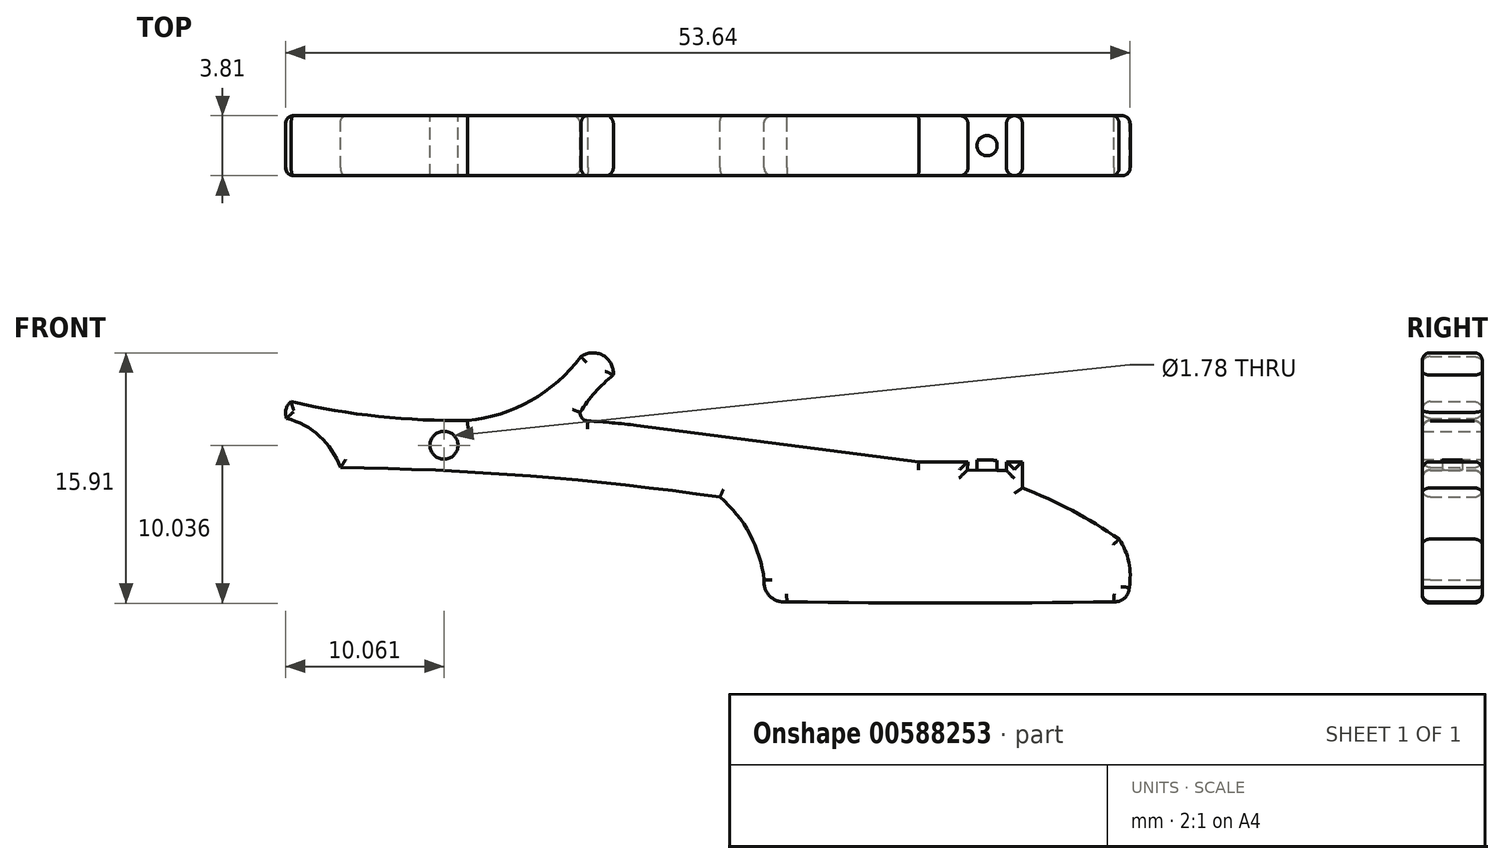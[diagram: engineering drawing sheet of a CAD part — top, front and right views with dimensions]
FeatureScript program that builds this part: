
annotation { "Feature Type Name" : "Feature", "Feature Type Description" : "" }
export const myFeature = defineFeature(function(context is Context, id is Id, definition is map)
    precondition{}
    {
        {
            var Q0;
            Q0=qCreatedBy(makeId("Front.planeOp"),FACE);
            var sketch = newSketch(context, id + "F0", { "sketchPlane" : qUnion([Q0])});
            skLineSegment(sketch, "E0", {"start": v(-47.34, 18.05) * mm, "end": v(-47.34, 18.05) * mm});
            skPoint(sketch, "E1", {"position": v(-38.73, 22.02) * mm});
            skArc(sketch, "E2", {"start": v(-38.9, 20.92) * mm, "mid": v(-39.55, 22.17) * mm, "end": v(-40.95, 22.1) * mm});
            skArc(sketch, "E3", {"start": v(-29.32, 7.9) * mm, "mid": v(-30.22, 10.8) * mm, "end": v(-32.13, 13.17) * mm});
            skArc(sketch, "E4", {"start": v(-29.32, 7.9) * mm, "mid": v(-28.93, 6.85) * mm, "end": v(-27.86, 6.53) * mm});
            skArc(sketch, "E5", {"start": v(-27.86, 6.53) * mm, "mid": v(-17.48, 6.43) * mm, "end": v(-7.1, 6.53) * mm});
            skArc(sketch, "E6", {"start": v(-7.1, 6.53) * mm, "mid": v(-6.41, 6.76) * mm, "end": v(-6.13, 7.44) * mm});
            skArc(sketch, "E7", {"start": v(-48.16, 18.05) * mm, "mid": v(-44.12, 19.3) * mm, "end": v(-40.95, 22.1) * mm});
            skLineSegment(sketch, "E8", {"start": v(-37.43, 17.72) * mm, "end": v(-19.5, 15.42) * mm});
            skArc(sketch, "E9", {"start": v(-6.13, 7.44) * mm, "mid": v(-6.16, 9.03) * mm, "end": v(-6.77, 10.5) * mm});
            skArc(sketch, "E10", {"start": v(-38.9, 20.92) * mm, "mid": v(-40.05, 19.83) * mm, "end": v(-41, 18.56) * mm});
            skArc(sketch, "E11", {"start": v(-37.43, 17.72) * mm, "mid": v(-38.97, 17.9) * mm, "end": v(-40.51, 18.01) * mm});
            skArc(sketch, "E12", {"start": v(-41, 18.56) * mm, "mid": v(-40.87, 18.18) * mm, "end": v(-40.51, 18.01) * mm});
            skArc(sketch, "E13", {"start": v(-59.35, 19.24) * mm, "mid": v(-53.8, 18.3) * mm, "end": v(-48.16, 18.05) * mm});
            skArc(sketch, "E14", {"start": v(-59.35, 19.24) * mm, "mid": v(-59.68, 18.76) * mm, "end": v(-59.64, 18.18) * mm});
            skArc(sketch, "E15", {"start": v(-56.23, 15.05) * mm, "mid": v(-57.55, 17.04) * mm, "end": v(-59.64, 18.18) * mm});
            skArc(sketch, "E16", {"start": v(-32.13, 13.17) * mm, "mid": v(-44.15, 14.5) * mm, "end": v(-56.23, 15.05) * mm});
            skPoint(sketch, "E17", {"position": v(-49.65, 16.47) * mm});
            skLineSegment(sketch, "E18", {"start": v(-12.9, 15.42) * mm, "end": v(-12.9, 13.76) * mm});
            skArc(sketch, "E19", {"start": v(-6.77, 10.5) * mm, "mid": v(-9.75, 12.31) * mm, "end": v(-12.9, 13.76) * mm});
            skLineSegment(sketch, "E20", {"start": v(-12.9, 15.42) * mm, "end": v(-13.92, 15.42) * mm});
            skLineSegment(sketch, "E21", {"start": v(-13.92, 15.42) * mm, "end": v(-13.93, 14.87) * mm});
            skLineSegment(sketch, "E22", {"start": v(-13.93, 14.87) * mm, "end": v(-16.4, 14.9) * mm});
            skLineSegment(sketch, "E23", {"start": v(-16.4, 14.9) * mm, "end": v(-16.37, 15.42) * mm});
            skLineSegment(sketch, "E24", {"start": v(-16.37, 15.42) * mm, "end": v(-19.5, 15.42) * mm});
            skSolve(sketch);
        }
        {
            var Q0;
            Q0=makeQuery(id+"F0.imprint","IMPRINT",FACE,{"disambiguationData":[TD([[makeQuery(id+"F0.imprint","IMPRINT",EDGE,{"derivedFrom":sQuery(id+"F0.wireOp",EDGE,"Z6wF5neN-Ii96-w33l-0QAA-09puhAKwVNem")}),1.0]])]});
            var Q1;
            {var subQ0=sQuery(id+"F0.wireOp",EDGE,"qjeVteD5-cl9v-Hz1g-wAoy-Im8fK0MNLn2P");Q1=makeQuery(id+"F0.imprint","IMPRINT",FACE,{"disambiguationData":[TD([[makeQuery(id+"F0.imprint","IMPRINT",EDGE,{"derivedFrom":subQ0}),1.0]])]});}
            var Q2;
            Q2=makeQuery(id+"F0.imprint","IMPRINT",FACE,{"disambiguationData":[TD([[makeQuery(id+"F0.imprint","IMPRINT",EDGE,{"derivedFrom":sQuery(id+"F0.wireOp",EDGE,"E2")}),1.0]])]});
            extrude(context, id + "F1", {"entities" : qUnion([Q0, Q1, Q2]), "depth" : 3.8 * mm, "offsetDistance" : 25.4 * mm});
        }
        {
            var Q0;
            Q0=makeQuery(id+"F1.opExtrude","CAP_FACE",FACE,{"disambiguationData":[OSD([sQuery(id+"F0.wireOp",EDGE,"E2"),sQuery(id+"F0.wireOp",EDGE,"xcBTiGL1-K37J-G7Q2-KfdZ-Ynig18PYwjIx"),sQuery(id+"F0.wireOp",EDGE,"E3"),sQuery(id+"F0.wireOp",EDGE,"E4"),sQuery(id+"F0.wireOp",EDGE,"E5"),sQuery(id+"F0.wireOp",EDGE,"E6"),sQuery(id+"F0.wireOp",EDGE,"E7"),sQuery(id+"F0.wireOp",EDGE,"J3uXdw90-iJFW-L0Le-SWdu-wUSDh88EqOZ0"),sQuery(id+"F0.wireOp",EDGE,"hGdytUsY-MjrS-cCVp-J9S7-tgxCRg4J04X1"),sQuery(id+"F0.wireOp",EDGE,"ds8ipJuK-Xwwi-Bh00-O7vx-r1XVzBg9BMgZ"),sQuery(id+"F0.wireOp",EDGE,"E8"),sQuery(id+"F0.wireOp",EDGE,"VuXbFIQG-ENT5-PDDP-iTfT-bwm7KxFRpuIf"),sQuery(id+"F0.wireOp",EDGE,"2HJuD3uH-Dv5W-Maqk-aKHw-hE9rkQbYQFsY"),sQuery(id+"F0.wireOp",EDGE,"35bAuxON-bHDy-JZCM-imzR-iOaWaIpl5IPb"),sQuery(id+"F0.wireOp",EDGE,"XMbSyPYu-U3Vw-C4fc-CisE-sYoG7PX9u947")])],"isStart":false});
            var Q1;
            Q1=makeQuery(id+"F1.opExtrude","CAP_FACE",FACE,{"disambiguationData":[OSD([sQuery(id+"F0.wireOp",EDGE,"E2"),sQuery(id+"F0.wireOp",EDGE,"E3"),sQuery(id+"F0.wireOp",EDGE,"E4"),sQuery(id+"F0.wireOp",EDGE,"E5"),sQuery(id+"F0.wireOp",EDGE,"E6"),sQuery(id+"F0.wireOp",EDGE,"E7"),sQuery(id+"F0.wireOp",EDGE,"E8"),sQuery(id+"F0.wireOp",EDGE,"nPg6tcf9-vbYi-KW5N-9vcZ-NgYAuYbe3bRj"),sQuery(id+"F0.wireOp",EDGE,"E9"),sQuery(id+"F0.wireOp",EDGE,"E10"),sQuery(id+"F0.wireOp",EDGE,"E11"),sQuery(id+"F0.wireOp",EDGE,"E12"),sQuery(id+"F0.wireOp",EDGE,"E13"),sQuery(id+"F0.wireOp",EDGE,"E14"),sQuery(id+"F0.wireOp",EDGE,"E15"),sQuery(id+"F0.wireOp",EDGE,"E16")])],"isStart":true});
            fillet(context, id + "F2", {"entities" : qUnion([Q0, Q1]), "radius" : 0.5 * mm, "tangentPropagation" : true, "allowEdgeOverflow" : false});
        }
        {
            var Q0;
            Q0=sQuery(id+"F0.wireOp",VERTEX,"d21cc25c-b378-4c89-b5f6-9ae40aecd30e");
            var Q1;
            Q1=sQuery(id+"F0.wireOp",VERTEX,"00dffb0d-e6b6-4c7a-ad87-2190a410a85d");
            var Q2;
            Q2=sQuery(id+"F0.wireOp",VERTEX,"E17");
            var Q3;
            Q3=makeQuery(id+"F1.opExtrude","SWEPT_BODY",BODY,{"disambiguationData":[OSD([sQuery(id+"F0.wireOp",EDGE,"E2"),sQuery(id+"F0.wireOp",EDGE,"E3"),sQuery(id+"F0.wireOp",EDGE,"E4"),sQuery(id+"F0.wireOp",EDGE,"E5"),sQuery(id+"F0.wireOp",EDGE,"E6"),sQuery(id+"F0.wireOp",EDGE,"E7"),sQuery(id+"F0.wireOp",EDGE,"E8"),sQuery(id+"F0.wireOp",EDGE,"nPg6tcf9-vbYi-KW5N-9vcZ-NgYAuYbe3bRj"),sQuery(id+"F0.wireOp",EDGE,"E9"),sQuery(id+"F0.wireOp",EDGE,"E10"),sQuery(id+"F0.wireOp",EDGE,"E11"),sQuery(id+"F0.wireOp",EDGE,"E12"),sQuery(id+"F0.wireOp",EDGE,"E13"),sQuery(id+"F0.wireOp",EDGE,"E14"),sQuery(id+"F0.wireOp",EDGE,"E15"),sQuery(id+"F0.wireOp",EDGE,"E16")])]});
            hole(context, id + "F3", {"style" : HoleStyle.SIMPLE, "endStyle" : HoleEndStyle.THROUGH, "oppositeDirection" : true, "holeDiameter" : 1.78 * mm, "majorDiameter" : 6.35 * mm, "isTappedThrough" : true, "tappedDepth" : 12.7 * mm, "tapClearance" : 3, "locations" : qUnion([Q0, Q1, Q2]), "scope" : qUnion([Q3])});
        }
        {
            var Q0;
            Q0=makeQuery(id+"F1.opExtrude","SWEPT_FACE",FACE,{"disambiguationData":[OSD([sQuery(id+"F0.wireOp",EDGE,"E22")])]});
            var sketch = newSketch(context, id + "F4", { "sketchPlane" : qUnion([Q0])});
            skCircle(sketch, "E25", {"center": v(-15.31, -1.9) * mm, "radius": 0.64 * mm});
            skPoint(sketch, "E25.centerSnap0", {"position": v(-15.31, -0.5) * mm});
            skPoint(sketch, "E25.centerSnap1", {"position": v(-16.55, -1.9) * mm});
            skSolve(sketch);
        }
        {
            var Q0;
            Q0=makeQuery(id+"F4.imprint","IMPRINT",FACE,{"disambiguationData":[TD([[makeQuery(id+"F4.imprint","IMPRINT",EDGE,{"derivedFrom":sQuery(id+"F4.wireOp",EDGE,"E25")}),1.0]])]});
            extrude(context, id + "F5", {"entities" : qUnion([Q0]), "operationType" : NewBodyOperationType.ADD, "depth" : 0.64 * mm, "offsetDistance" : 25.4 * mm});
        }
    });
